# Revit family: Lighting_Ceiling-Mounted_Focus-Lighting_Pelee-Downlight
name_source: partatom
category: Lighting Fixtures
revit_build: Autodesk Revit 2015 (Build: 20140903_1530(x64)
units: mm (PartAtom-declared; Revit-internal decimal feet)

## types (1)
- 2830-2927
    BIMobject category = Ceiling Mounted
    BIMobject category code = lighting-ceiling-mounted
    BIMobject main category = Lighting
    BIMobject main category code = lighting
    BOSUseNativeGeometries = 1
    Brand url = http://focus-lighting.dk
    Built-in height = min 90 mm from lower ceiling edge
    Classification = IP20 class I
    Clearances = Horizontally min 45 mm
    Color Filter = 16777215
    Colour = White 99891D90
    Colour accuracy = 3 steps SDCM
    Colour rendering = min 90 Ra
    Connection = Max two cables 5 x 1.5 mm2 into 5-pole terminal block 2 x 2.5 mm2
    Cut-out = Ø149-154 mm in 6-15 mm plates; Ø155-158 mm in 15-35 mm plates
    Design country = Denmark
    Dimming = without dimming
    Dimming Lamp Color Temperature Shift = <None>
    Driver = Helvar LED driver 500-700 mA
    Edition number = 1
    Energy consumption = 12
    IFC Classification = Lamp
    Manufacturer country = Denmark
    Manufacturer name = Focus Lighting
    Masterformat 2014 Code = 12 43 13
    Masterformat 2014 Description = Lamps
    Material = Cast aluminium
    Material main = Aluminium
    Material secondary = Polycarbonate
    Mounting = To be recessed
    NBS Reference Code = 49
    NBS Reference Description = Luminaires And Lamps
    Nominal height = 0
    Nominal width = 0
    OmniClass Code = 23-35 45 15
    OmniClass Description = Lamps
    Operational life = min 100.000 hours at ta max 25°C L80B10
    Output ratio = Output ratio
    Product Guid = 442520c9-aacd-4886-9d05-c88ee0c39426
    Product SKU = pelee-downlight
    Product data url = https://bimobject.com
    Product family = Outdoor
    Product group = Downlight
    Product name = Pelee Downlight
    Product url = http://www.focus-lighting.dk
    QR code = http://bimobject.com
    Tilt Angle = 90.00°
    UNSPSC Code = 391016
    Uniclass 1.4 Code = L7474
    Uniclass 1.4 Description = Lamps
    Uniclass 2.0 Code = PR-49
    Uniclass 2.0 Description = Luminaires and Lamps
    Uniclass 2015 Code = Pr_70_70_46
    Uniclass 2015 Name = Lamps
    Weight = 0.85 kg
    Weight Net (Kg) = 0

## geometry (parser evidence)
native form markers: Sweep x2
no freeform markers — native parametric forms only
